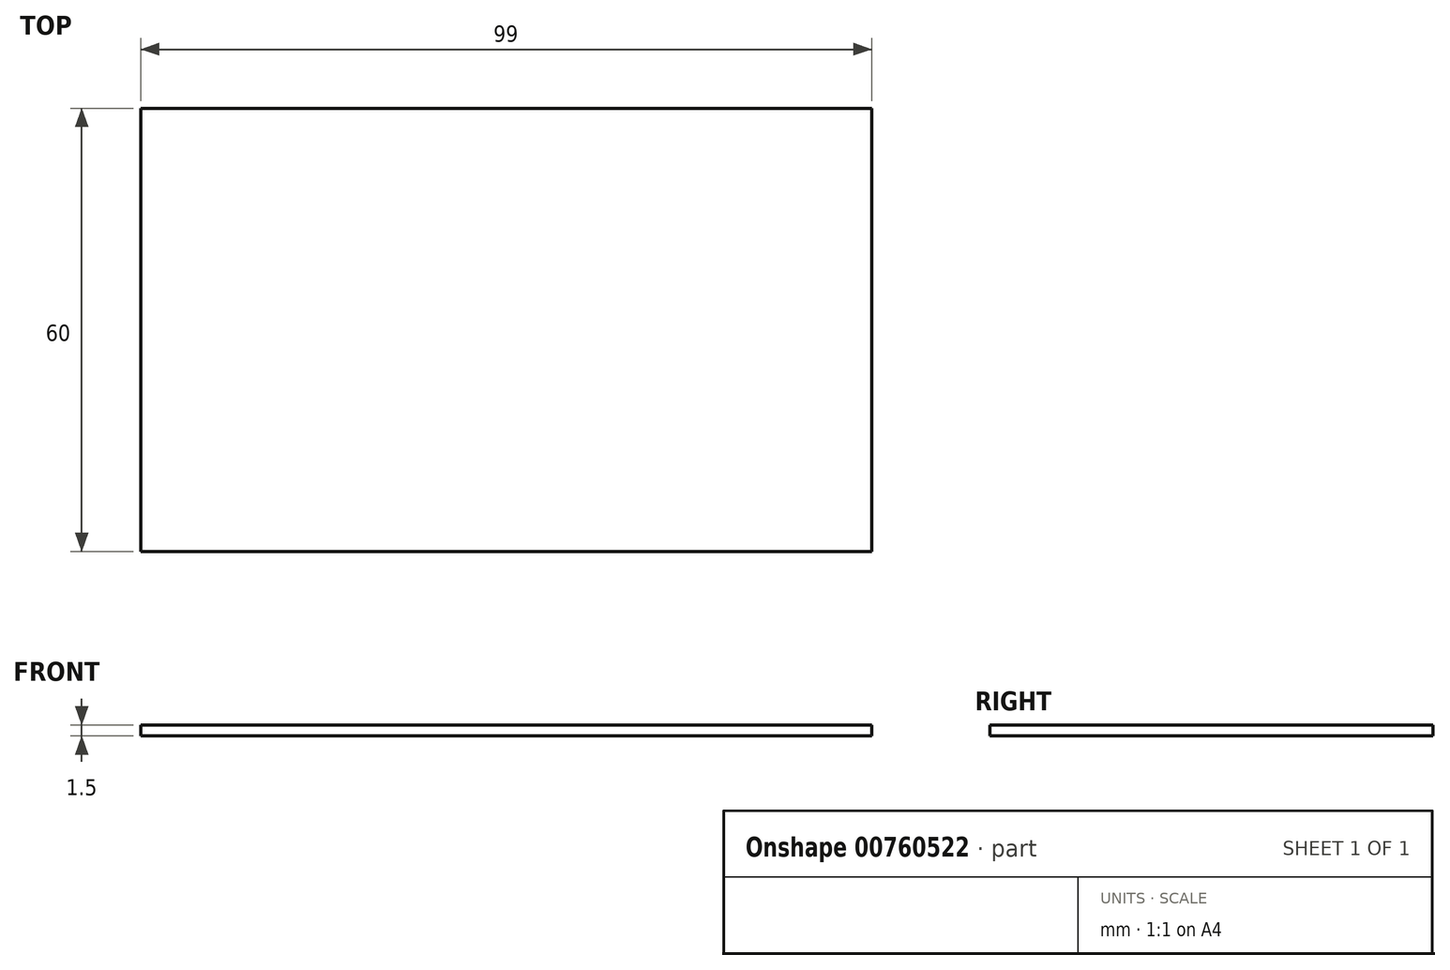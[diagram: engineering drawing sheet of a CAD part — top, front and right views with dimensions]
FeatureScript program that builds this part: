
annotation { "Feature Type Name" : "Feature", "Feature Type Description" : "" }
export const myFeature = defineFeature(function(context is Context, id is Id, definition is map)
    precondition{}
    {
        {
            var Q0;
            Q0=qCreatedBy(makeId("Top.planeOp"),FACE);
            var sketch = newSketch(context, id + "F0", { "sketchPlane" : qUnion([Q0])});
            skLineSegment(sketch, "E0.bottom", {"start": v(-49.5, -30) * mm, "end": v(49.5, -30) * mm});
            skLineSegment(sketch, "E0.top", {"start": v(-49.5, 30) * mm, "end": v(49.5, 30) * mm});
            skLineSegment(sketch, "E0.left", {"start": v(-49.5, -30) * mm, "end": v(-49.5, 30) * mm});
            skLineSegment(sketch, "E0.right", {"start": v(49.5, -30) * mm, "end": v(49.5, 30) * mm});
            skPoint(sketch, "E0.middle", {"position": v(0, 0) * mm});
            skSolve(sketch);
        }
        {
            var Q0;
            Q0 = qSketchRegion(id + "F0", true);
            extrude(context, id + "F1", {"entities" : qUnion([Q0]), "depth" : 1.5 * mm, "offsetDistance" : 25 * mm});
        }
    });
